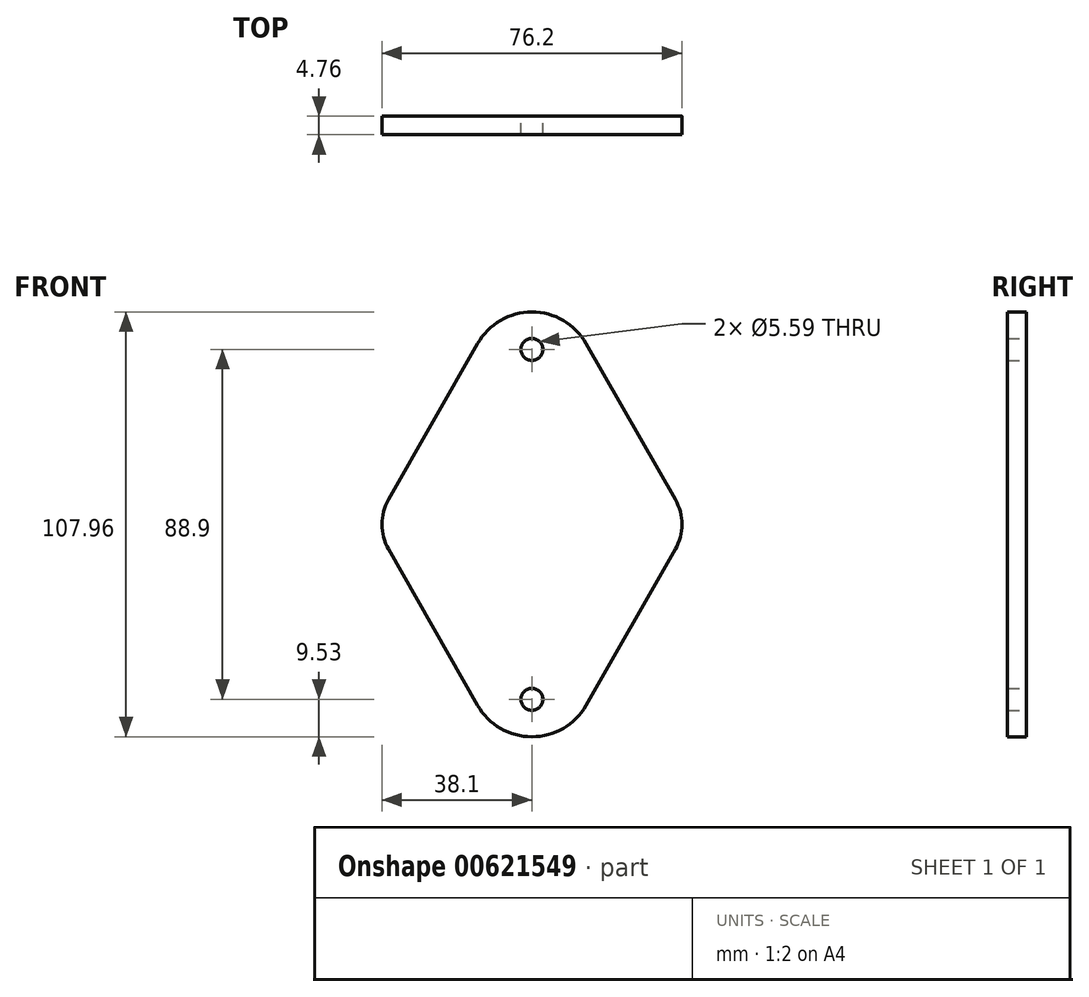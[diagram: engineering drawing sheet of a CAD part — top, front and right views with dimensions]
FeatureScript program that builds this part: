
annotation { "Feature Type Name" : "Feature", "Feature Type Description" : "" }
export const myFeature = defineFeature(function(context is Context, id is Id, definition is map)
    precondition{}
    {
        {
            var Q0;
            Q0=qCreatedBy(makeId("Front.planeOp"),FACE);
            var sketch = newSketch(context, id + "F0", { "sketchPlane" : qUnion([Q0])});
            skLineSegment(sketch, "E0", {"start": v(-13.79, 45.97) * mm, "end": v(-36.43, 6.3) * mm});
            skLineSegment(sketch, "E1", {"start": v(-36.43, -6.3) * mm, "end": v(-13.79, -45.97) * mm});
            skLineSegment(sketch, "E2", {"start": v(13.79, 45.97) * mm, "end": v(36.43, 6.3) * mm});
            skLineSegment(sketch, "E3", {"start": v(36.43, -6.3) * mm, "end": v(13.79, -45.97) * mm});
            skArc(sketch, "E4", {"start": v(-13.79, 45.97) * mm, "mid": v(0, 53.98) * mm, "end": v(13.79, 45.97) * mm});
            skArc(sketch, "E5", {"start": v(-13.79, -45.97) * mm, "mid": v(0, -53.98) * mm, "end": v(13.79, -45.97) * mm});
            skArc(sketch, "E6", {"start": v(-36.43, 6.3) * mm, "mid": v(-38.1, 0) * mm, "end": v(-36.43, -6.3) * mm});
            skArc(sketch, "E7", {"start": v(36.43, 6.3) * mm, "mid": v(38.1, 0) * mm, "end": v(36.43, -6.3) * mm});
            skCircle(sketch, "E8", {"center": v(0, 44.45) * mm, "radius": 2.8 * mm});
            skCircle(sketch, "E9", {"center": v(0, -44.45) * mm, "radius": 2.8 * mm});
            skPoint(sketch, "E10", {"position": v(-38.1, 0) * mm});
            skPoint(sketch, "E11", {"position": v(38.1, 0) * mm});
            skPoint(sketch, "E12", {"position": v(0, -53.98) * mm});
            skPoint(sketch, "E13", {"position": v(0, 53.98) * mm});
            skSolve(sketch);
        }
        {
            var Q0;
            Q0=makeQuery(id+"F0.imprint","IMPRINT",FACE,{"disambiguationData":[TD([[makeQuery(id+"F0.imprint","IMPRINT",EDGE,{"derivedFrom":sQuery(id+"F0.wireOp",EDGE,"E0")}),1.0]])]});
            extrude(context, id + "F1", {"entities" : qUnion([Q0]), "endBound" : BoundingType.SYMMETRIC, "depth" : 4.76 * mm, "offsetDistance" : 25.4 * mm});
        }
    });
